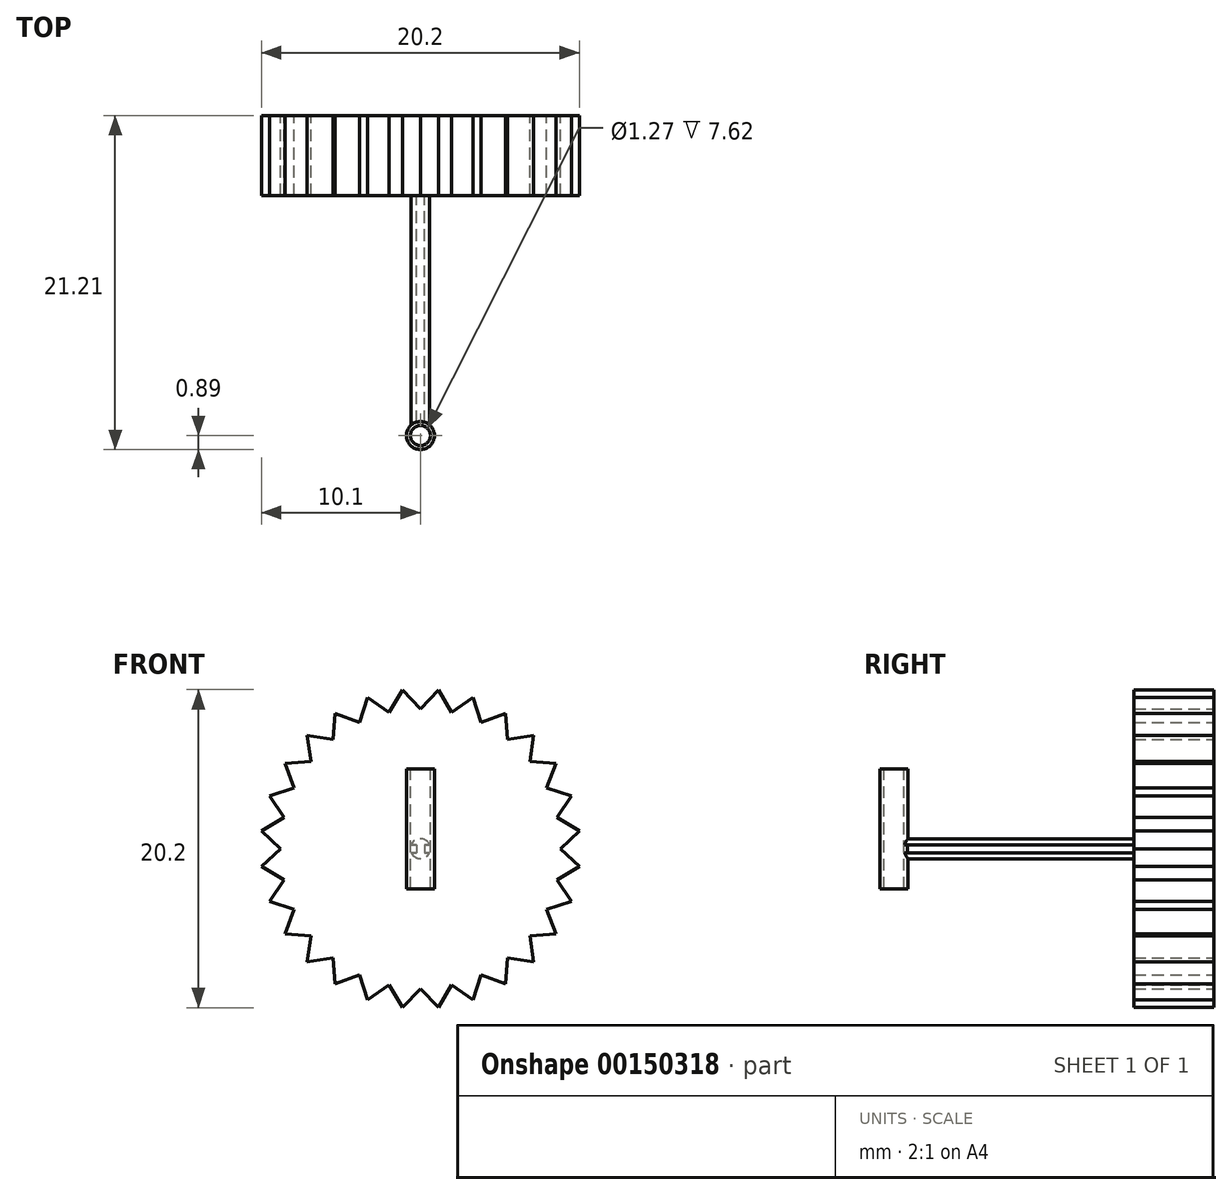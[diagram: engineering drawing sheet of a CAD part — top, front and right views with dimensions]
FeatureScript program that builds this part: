
annotation { "Feature Type Name" : "Feature", "Feature Type Description" : "" }
export const myFeature = defineFeature(function(context is Context, id is Id, definition is map)
    precondition{}
    {
        {
            var Q0;
            Q0=qCreatedBy(makeId("Front.planeOp"),FACE);
            var sketch = newSketch(context, id + "F0", { "sketchPlane" : qUnion([Q0])});
            skCircle(sketch, "E0", {"center": v(0, 0) * mm, "radius": 10.16 * mm});
            skCircle(sketch, "E1", {"center": v(0, 0) * mm, "radius": 8.9 * mm});
            skLineSegment(sketch, "E2", {"start": v(0, 0) * mm, "end": v(0, 8.9) * mm});
            skLineSegment(sketch, "E3", {"start": v(0, 8.9) * mm, "end": v(0, -8.9) * mm});
            skLineSegment(sketch, "E4", {"start": v(0, -8.9) * mm, "end": v(-1.14, -10.1) * mm});
            skLineSegment(sketch, "E5", {"start": v(-1.14, -10.1) * mm, "end": v(-1.98, -8.67) * mm});
            skLineSegment(sketch, "E6", {"start": v(-1.98, -8.67) * mm, "end": v(0, 0) * mm});
            skLineSegment(sketch, "E7", {"start": v(-1.14, -10.1) * mm, "end": v(0, 0) * mm});
            skLineSegment(sketch, "E8", {"start": v(0, 0) * mm, "end": v(-3.36, -9.59) * mm});
            skLineSegment(sketch, "E9", {"start": v(0, 0) * mm, "end": v(-3.86, -8) * mm});
            skLineSegment(sketch, "E10", {"start": v(-3.86, -8) * mm, "end": v(-3.36, -9.59) * mm});
            skLineSegment(sketch, "E11", {"start": v(-1.98, -8.67) * mm, "end": v(-3.36, -9.59) * mm});
            skLineSegment(sketch, "E12.MirrorCS", {"start": v(-3.86, -8) * mm, "end": v(-5.4, -8.6) * mm});
            skLineSegment(sketch, "E13.MirrorCS", {"start": v(0, 0) * mm, "end": v(-5.4, -8.6) * mm});
            skLineSegment(sketch, "E14.MirrorCS", {"start": v(-5.54, -6.95) * mm, "end": v(-5.4, -8.6) * mm});
            skLineSegment(sketch, "E15.MirrorCS", {"start": v(-7.18, -7.18) * mm, "end": v(-5.54, -6.95) * mm});
            skLineSegment(sketch, "E16.MirrorCS", {"start": v(-5.54, -6.95) * mm, "end": v(0, 0) * mm});
            skLineSegment(sketch, "E17.MirrorCS", {"start": v(-7.18, -7.18) * mm, "end": v(0, 0) * mm});
            skLineSegment(sketch, "E18.MirrorCS", {"start": v(-6.95, -5.54) * mm, "end": v(-7.18, -7.18) * mm});
            skLineSegment(sketch, "E19.MirrorCS", {"start": v(6.95, 5.54) * mm, "end": v(-6.95, -5.54) * mm});
            skLineSegment(sketch, "E20.MirrorCS", {"start": v(-6.95, -5.54) * mm, "end": v(-8.6, -5.4) * mm});
            skLineSegment(sketch, "E21.MirrorCS", {"start": v(-8.6, -5.4) * mm, "end": v(0, 0) * mm});
            skLineSegment(sketch, "E22.MirrorCS", {"start": v(-8.6, -5.4) * mm, "end": v(-8, -3.86) * mm});
            skLineSegment(sketch, "E23.MirrorCS", {"start": v(-8, -3.86) * mm, "end": v(0, 0) * mm});
            skLineSegment(sketch, "E24.MirrorCS", {"start": v(-8, -3.86) * mm, "end": v(-9.59, -3.36) * mm});
            skLineSegment(sketch, "E25.MirrorCS", {"start": v(0, 0) * mm, "end": v(-9.59, -3.36) * mm});
            skLineSegment(sketch, "E26.MirrorCS", {"start": v(-8.67, -1.98) * mm, "end": v(-9.59, -3.36) * mm});
            skLineSegment(sketch, "E27.MirrorCS", {"start": v(0, 0) * mm, "end": v(-8.67, -1.98) * mm});
            skLineSegment(sketch, "E28.MirrorCS", {"start": v(-8.67, -1.98) * mm, "end": v(-10.1, -1.14) * mm});
            skLineSegment(sketch, "E29.MirrorCS", {"start": v(0, 0) * mm, "end": v(-10.1, -1.14) * mm});
            skLineSegment(sketch, "E30.MirrorCS", {"start": v(-8.9, 0) * mm, "end": v(-10.1, -1.14) * mm});
            skLineSegment(sketch, "E31.MirrorCS", {"start": v(-8.9, 0) * mm, "end": v(0, 0) * mm});
            skLineSegment(sketch, "E32.MirrorCS", {"start": v(-10.1, 1.14) * mm, "end": v(-8.9, 0) * mm});
            skLineSegment(sketch, "E33.MirrorCS", {"start": v(-10.1, 1.14) * mm, "end": v(0, 0) * mm});
            skLineSegment(sketch, "E34.MirrorCS", {"start": v(-8.67, 1.98) * mm, "end": v(-10.1, 1.14) * mm});
            skLineSegment(sketch, "E35.MirrorCS", {"start": v(8.67, -1.98) * mm, "end": v(-8.67, 1.98) * mm});
            skLineSegment(sketch, "E36.MirrorCS", {"start": v(-8.67, 1.98) * mm, "end": v(-9.59, 3.36) * mm});
            skLineSegment(sketch, "E37.MirrorCS", {"start": v(-9.59, 3.36) * mm, "end": v(0, 0) * mm});
            skLineSegment(sketch, "E38.MirrorCS", {"start": v(-9.59, 3.36) * mm, "end": v(-8, 3.86) * mm});
            skLineSegment(sketch, "E39.MirrorCS", {"start": v(-8, 3.86) * mm, "end": v(0, 0) * mm});
            skLineSegment(sketch, "E40.MirrorCS", {"start": v(-8, 3.86) * mm, "end": v(-8.6, 5.4) * mm});
            skLineSegment(sketch, "E41.MirrorCS", {"start": v(0, 0) * mm, "end": v(-8.6, 5.4) * mm});
            skLineSegment(sketch, "E42.MirrorCS", {"start": v(-6.95, 5.54) * mm, "end": v(-8.6, 5.4) * mm});
            skLineSegment(sketch, "E43.MirrorCS", {"start": v(0, 0) * mm, "end": v(-6.95, 5.54) * mm});
            skLineSegment(sketch, "E44.MirrorCS", {"start": v(-6.95, 5.54) * mm, "end": v(-7.18, 7.18) * mm});
            skLineSegment(sketch, "E45.MirrorCS", {"start": v(0, 0) * mm, "end": v(-7.18, 7.18) * mm});
            skLineSegment(sketch, "E46.MirrorCS", {"start": v(-5.54, 6.95) * mm, "end": v(-7.18, 7.18) * mm});
            skLineSegment(sketch, "E47.MirrorCS", {"start": v(-5.54, 6.95) * mm, "end": v(0, 0) * mm});
            skLineSegment(sketch, "E48.MirrorCS", {"start": v(-5.4, 8.6) * mm, "end": v(-5.54, 6.95) * mm});
            skLineSegment(sketch, "E49.MirrorCS", {"start": v(-5.4, 8.6) * mm, "end": v(0, 0) * mm});
            skLineSegment(sketch, "E50.MirrorCS", {"start": v(-3.86, 8) * mm, "end": v(-5.4, 8.6) * mm});
            skLineSegment(sketch, "E51.MirrorCS", {"start": v(3.86, -8) * mm, "end": v(-3.86, 8) * mm});
            skLineSegment(sketch, "E52.MirrorCS", {"start": v(-3.86, 8) * mm, "end": v(-3.36, 9.59) * mm});
            skLineSegment(sketch, "E53.MirrorCS", {"start": v(-3.36, 9.59) * mm, "end": v(0, 0) * mm});
            skLineSegment(sketch, "E54.MirrorCS", {"start": v(-3.36, 9.59) * mm, "end": v(-1.98, 8.67) * mm});
            skLineSegment(sketch, "E55.MirrorCS", {"start": v(-1.98, 8.67) * mm, "end": v(0, 0) * mm});
            skLineSegment(sketch, "E56.MirrorCS", {"start": v(-1.98, 8.67) * mm, "end": v(-1.14, 10.1) * mm});
            skLineSegment(sketch, "E57.MirrorCS", {"start": v(0, 0) * mm, "end": v(-1.14, 10.1) * mm});
            skLineSegment(sketch, "E58.MirrorCS", {"start": v(0, 8.89) * mm, "end": v(-1.14, 10.1) * mm});
            skLineSegment(sketch, "E59.MirrorCS", {"start": v(0, 0) * mm, "end": v(0, 8.89) * mm});
            skLineSegment(sketch, "E60.MirrorCS", {"start": v(0, 8.89) * mm, "end": v(1.14, 10.1) * mm});
            skLineSegment(sketch, "E61.MirrorCS", {"start": v(0, 0) * mm, "end": v(1.14, 10.1) * mm});
            skLineSegment(sketch, "E62.MirrorCS", {"start": v(1.98, 8.67) * mm, "end": v(1.14, 10.1) * mm});
            skLineSegment(sketch, "E63.MirrorCS", {"start": v(1.98, 8.67) * mm, "end": v(0, 0) * mm});
            skLineSegment(sketch, "E64.MirrorCS", {"start": v(3.36, 9.59) * mm, "end": v(1.98, 8.67) * mm});
            skLineSegment(sketch, "E65.MirrorCS", {"start": v(3.36, 9.59) * mm, "end": v(0, 0) * mm});
            skLineSegment(sketch, "E66.MirrorCS", {"start": v(3.86, 8) * mm, "end": v(3.36, 9.59) * mm});
            skLineSegment(sketch, "E67.MirrorCS", {"start": v(-3.86, -8) * mm, "end": v(3.86, 8) * mm});
            skLineSegment(sketch, "E68.MirrorCS", {"start": v(3.86, 8) * mm, "end": v(5.4, 8.6) * mm});
            skLineSegment(sketch, "E69.MirrorCS", {"start": v(5.4, 8.6) * mm, "end": v(0, 0) * mm});
            skLineSegment(sketch, "E70.MirrorCS", {"start": v(5.4, 8.6) * mm, "end": v(5.54, 6.95) * mm});
            skLineSegment(sketch, "E71.MirrorCS", {"start": v(5.54, 6.95) * mm, "end": v(0, 0) * mm});
            skLineSegment(sketch, "E72.MirrorCS", {"start": v(5.54, 6.95) * mm, "end": v(7.18, 7.18) * mm});
            skLineSegment(sketch, "E73.MirrorCS", {"start": v(0, 0) * mm, "end": v(7.18, 7.18) * mm});
            skLineSegment(sketch, "E74.MirrorCS", {"start": v(6.95, 5.54) * mm, "end": v(7.18, 7.18) * mm});
            skLineSegment(sketch, "E75.MirrorCS", {"start": v(6.95, 5.54) * mm, "end": v(8.6, 5.4) * mm});
            skLineSegment(sketch, "E76.MirrorCS", {"start": v(0, 0) * mm, "end": v(8.6, 5.4) * mm});
            skLineSegment(sketch, "E77.MirrorCS", {"start": v(8, 3.86) * mm, "end": v(8.6, 5.4) * mm});
            skLineSegment(sketch, "E78.MirrorCS", {"start": v(8, 3.86) * mm, "end": v(0, 0) * mm});
            skLineSegment(sketch, "E79.MirrorCS", {"start": v(9.59, 3.36) * mm, "end": v(8, 3.86) * mm});
            skLineSegment(sketch, "E80.MirrorCS", {"start": v(9.59, 3.36) * mm, "end": v(0, 0) * mm});
            skLineSegment(sketch, "E81.MirrorCS", {"start": v(8.67, 1.98) * mm, "end": v(9.59, 3.36) * mm});
            skLineSegment(sketch, "E82.MirrorCS", {"start": v(-8.67, -1.98) * mm, "end": v(8.67, 1.98) * mm});
            skLineSegment(sketch, "E83.MirrorCS", {"start": v(8.67, 1.98) * mm, "end": v(10.1, 1.14) * mm});
            skLineSegment(sketch, "E84.MirrorCS", {"start": v(10.1, 1.14) * mm, "end": v(8.9, 0) * mm});
            skLineSegment(sketch, "E85.MirrorCS", {"start": v(10.1, 1.14) * mm, "end": v(0, 0) * mm});
            skLineSegment(sketch, "E86.MirrorCS", {"start": v(8.9, 0) * mm, "end": v(0, 0) * mm});
            skLineSegment(sketch, "E87.MirrorCS", {"start": v(8.9, 0) * mm, "end": v(10.1, -1.14) * mm});
            skLineSegment(sketch, "E88.MirrorCS", {"start": v(0, 0) * mm, "end": v(10.1, -1.14) * mm});
            skLineSegment(sketch, "E89.MirrorCS", {"start": v(8.67, -1.98) * mm, "end": v(10.1, -1.14) * mm});
            skLineSegment(sketch, "E90.MirrorCS", {"start": v(0, 0) * mm, "end": v(8.67, -1.98) * mm});
            skLineSegment(sketch, "E91.MirrorCS", {"start": v(8.67, -1.98) * mm, "end": v(9.59, -3.36) * mm});
            skLineSegment(sketch, "E92.MirrorCS", {"start": v(0, 0) * mm, "end": v(9.59, -3.36) * mm});
            skLineSegment(sketch, "E93.MirrorCS", {"start": v(8, -3.86) * mm, "end": v(9.59, -3.36) * mm});
            skLineSegment(sketch, "E94.MirrorCS", {"start": v(8, -3.86) * mm, "end": v(0, 0) * mm});
            skLineSegment(sketch, "E95.MirrorCS", {"start": v(8.6, -5.4) * mm, "end": v(8, -3.86) * mm});
            skLineSegment(sketch, "E96.MirrorCS", {"start": v(8.6, -5.4) * mm, "end": v(0, 0) * mm});
            skLineSegment(sketch, "E97.MirrorCS", {"start": v(6.95, -5.54) * mm, "end": v(8.6, -5.4) * mm});
            skLineSegment(sketch, "E98.MirrorCS", {"start": v(-6.95, 5.54) * mm, "end": v(6.95, -5.54) * mm});
            skLineSegment(sketch, "E99.MirrorCS", {"start": v(6.95, -5.54) * mm, "end": v(7.18, -7.18) * mm});
            skLineSegment(sketch, "E100.MirrorCS", {"start": v(7.18, -7.18) * mm, "end": v(0, 0) * mm});
            skLineSegment(sketch, "E101.MirrorCS", {"start": v(7.18, -7.18) * mm, "end": v(5.54, -6.95) * mm});
            skLineSegment(sketch, "E102.MirrorCS", {"start": v(5.54, -6.95) * mm, "end": v(0, 0) * mm});
            skLineSegment(sketch, "E103.MirrorCS", {"start": v(5.54, -6.95) * mm, "end": v(5.4, -8.6) * mm});
            skLineSegment(sketch, "E104.MirrorCS", {"start": v(0, 0) * mm, "end": v(5.4, -8.6) * mm});
            skLineSegment(sketch, "E105.MirrorCS", {"start": v(3.86, -8) * mm, "end": v(5.4, -8.6) * mm});
            skLineSegment(sketch, "E106.MirrorCS", {"start": v(0, 0) * mm, "end": v(3.86, -8) * mm});
            skLineSegment(sketch, "E107.MirrorCS", {"start": v(3.86, -8) * mm, "end": v(3.36, -9.59) * mm});
            skLineSegment(sketch, "E108.MirrorCS", {"start": v(1.98, -8.67) * mm, "end": v(3.36, -9.59) * mm});
            skLineSegment(sketch, "E109.MirrorCS", {"start": v(0, 0) * mm, "end": v(3.36, -9.59) * mm});
            skLineSegment(sketch, "E110.MirrorCS", {"start": v(1.98, -8.67) * mm, "end": v(0, 0) * mm});
            skLineSegment(sketch, "E111.MirrorCS", {"start": v(1.14, -10.1) * mm, "end": v(1.98, -8.67) * mm});
            skLineSegment(sketch, "E112.MirrorCS", {"start": v(1.14, -10.1) * mm, "end": v(0, 0) * mm});
            skLineSegment(sketch, "E113.MirrorCS", {"start": v(0, -8.9) * mm, "end": v(1.14, -10.1) * mm});
            skSolve(sketch);
        }
        {
            var Q0;
            {var subQ0=sQuery(id+"F0.wireOp",EDGE,"E51.MirrorCS");Q0=makeQuery(id+"F0.imprint","IMPRINT",FACE,{"disambiguationData":[TD([[makeQuery(id+"F0.imprint","IMPRINT",EDGE,{"derivedFrom":subQ0}),1.0]])]});}
            var Q1;
            {var subQ0=sQuery(id+"F0.wireOp",EDGE,"E47.MirrorCS");Q1=makeQuery(id+"F0.imprint","IMPRINT",FACE,{"disambiguationData":[TD([[makeQuery(id+"F0.imprint","IMPRINT",EDGE,{"derivedFrom":subQ0}),1.0]])]});}
            var Q2;
            {var subQ0=sQuery(id+"F0.wireOp",EDGE,"E48.MirrorCS");Q2=makeQuery(id+"F0.imprint","IMPRINT",FACE,{"disambiguationData":[TD([[makeQuery(id+"F0.imprint","IMPRINT",EDGE,{"derivedFrom":subQ0}),1.0]])]});}
            var Q3;
            {var subQ0=sQuery(id+"F0.wireOp",EDGE,"E50.MirrorCS");Q3=makeQuery(id+"F0.imprint","IMPRINT",FACE,{"disambiguationData":[TD([[makeQuery(id+"F0.imprint","IMPRINT",EDGE,{"derivedFrom":subQ0}),1.0]])]});}
            var Q4;
            {var subQ0=sQuery(id+"F0.wireOp",EDGE,"E52.MirrorCS");Q4=makeQuery(id+"F0.imprint","IMPRINT",FACE,{"disambiguationData":[TD([[makeQuery(id+"F0.imprint","IMPRINT",EDGE,{"derivedFrom":subQ0}),-1.0]])]});}
            var Q5;
            {var subQ0=sQuery(id+"F0.wireOp",EDGE,"E54.MirrorCS");Q5=makeQuery(id+"F0.imprint","IMPRINT",FACE,{"disambiguationData":[TD([[makeQuery(id+"F0.imprint","IMPRINT",EDGE,{"derivedFrom":subQ0}),-1.0]])]});}
            var Q6;
            {var subQ0=sQuery(id+"F0.wireOp",EDGE,"E55.MirrorCS");Q6=makeQuery(id+"F0.imprint","IMPRINT",FACE,{"disambiguationData":[TD([[makeQuery(id+"F0.imprint","IMPRINT",EDGE,{"derivedFrom":subQ0}),-1.0]])]});}
            var Q7;
            {var subQ0=sQuery(id+"F0.wireOp",EDGE,"E51.MirrorCS");Q7=makeQuery(id+"F0.imprint","IMPRINT",FACE,{"disambiguationData":[TD([[makeQuery(id+"F0.imprint","IMPRINT",EDGE,{"derivedFrom":subQ0}),-1.0]])]});}
            var Q8;
            {var subQ1=sQuery(id+"F0.wireOp",EDGE,"E1");var subQ3=sQuery(id+"F0.wireOp",EDGE,"E57.MirrorCS");var subQ4=makeQuery(id+"F0.imprint","INTERSECT",VERTEX,{"derivedFrom":[subQ1,subQ3]});Q8=makeQuery(id+"F0.imprint","IMPRINT",FACE,{"disambiguationData":[TD([[makeQuery(id+"F0.imprint","IMPRINT",EDGE,{"disambiguationData":[TD([[subQ4,1.0]])],"derivedFrom":subQ1}),1.0]])]});}
            var Q9;
            {var subQ0=sQuery(id+"F0.wireOp",EDGE,"E58.MirrorCS");Q9=makeQuery(id+"F0.imprint","IMPRINT",FACE,{"disambiguationData":[TD([[makeQuery(id+"F0.imprint","IMPRINT",EDGE,{"derivedFrom":subQ0}),1.0]])]});}
            var Q10;
            {var subQ0=sQuery(id+"F0.wireOp",EDGE,"E56.MirrorCS");Q10=makeQuery(id+"F0.imprint","IMPRINT",FACE,{"disambiguationData":[TD([[makeQuery(id+"F0.imprint","IMPRINT",EDGE,{"derivedFrom":subQ0}),-1.0]])]});}
            var Q11;
            {var subQ0=sQuery(id+"F0.wireOp",EDGE,"E55.MirrorCS");Q11=makeQuery(id+"F0.imprint","IMPRINT",FACE,{"disambiguationData":[TD([[makeQuery(id+"F0.imprint","IMPRINT",EDGE,{"derivedFrom":subQ0}),1.0]])]});}
            var Q12;
            {var subQ0=sQuery(id+"F0.wireOp",EDGE,"E47.MirrorCS");Q12=makeQuery(id+"F0.imprint","IMPRINT",FACE,{"disambiguationData":[TD([[makeQuery(id+"F0.imprint","IMPRINT",EDGE,{"derivedFrom":subQ0}),-1.0]])]});}
            var Q13;
            {var subQ0=sQuery(id+"F0.wireOp",EDGE,"E46.MirrorCS");Q13=makeQuery(id+"F0.imprint","IMPRINT",FACE,{"disambiguationData":[TD([[makeQuery(id+"F0.imprint","IMPRINT",EDGE,{"derivedFrom":subQ0}),1.0]])]});}
            var Q14;
            {var subQ1=sQuery(id+"F0.wireOp",EDGE,"E1");var subQ3=sQuery(id+"F0.wireOp",EDGE,"E45.MirrorCS");var subQ4=makeQuery(id+"F0.imprint","INTERSECT",VERTEX,{"derivedFrom":[subQ1,subQ3]});Q14=makeQuery(id+"F0.imprint","IMPRINT",FACE,{"disambiguationData":[TD([[makeQuery(id+"F0.imprint","IMPRINT",EDGE,{"disambiguationData":[TD([[subQ4,-1.0]])],"derivedFrom":subQ1}),1.0]])]});}
            var Q15;
            {var subQ0=sQuery(id+"F0.wireOp",EDGE,"E44.MirrorCS");Q15=makeQuery(id+"F0.imprint","IMPRINT",FACE,{"disambiguationData":[TD([[makeQuery(id+"F0.imprint","IMPRINT",EDGE,{"derivedFrom":subQ0}),-1.0]])]});}
            var Q16;
            {var subQ1=sQuery(id+"F0.wireOp",EDGE,"E1");var subQ3=sQuery(id+"F0.wireOp",EDGE,"E41.MirrorCS");var subQ4=makeQuery(id+"F0.imprint","INTERSECT",VERTEX,{"derivedFrom":[subQ1,subQ3]});Q16=makeQuery(id+"F0.imprint","IMPRINT",FACE,{"disambiguationData":[TD([[makeQuery(id+"F0.imprint","IMPRINT",EDGE,{"disambiguationData":[TD([[subQ4,1.0]])],"derivedFrom":subQ1}),1.0]])]});}
            var Q17;
            {var subQ0=sQuery(id+"F0.wireOp",EDGE,"E42.MirrorCS");Q17=makeQuery(id+"F0.imprint","IMPRINT",FACE,{"disambiguationData":[TD([[makeQuery(id+"F0.imprint","IMPRINT",EDGE,{"derivedFrom":subQ0}),1.0]])]});}
            var Q18;
            {var subQ0=sQuery(id+"F0.wireOp",EDGE,"E40.MirrorCS");Q18=makeQuery(id+"F0.imprint","IMPRINT",FACE,{"disambiguationData":[TD([[makeQuery(id+"F0.imprint","IMPRINT",EDGE,{"derivedFrom":subQ0}),-1.0]])]});}
            var Q19;
            {var subQ0=sQuery(id+"F0.wireOp",EDGE,"E39.MirrorCS");Q19=makeQuery(id+"F0.imprint","IMPRINT",FACE,{"disambiguationData":[TD([[makeQuery(id+"F0.imprint","IMPRINT",EDGE,{"derivedFrom":subQ0}),1.0]])]});}
            var Q20;
            {var subQ0=sQuery(id+"F0.wireOp",EDGE,"E39.MirrorCS");Q20=makeQuery(id+"F0.imprint","IMPRINT",FACE,{"disambiguationData":[TD([[makeQuery(id+"F0.imprint","IMPRINT",EDGE,{"derivedFrom":subQ0}),-1.0]])]});}
            var Q21;
            {var subQ0=sQuery(id+"F0.wireOp",EDGE,"E38.MirrorCS");Q21=makeQuery(id+"F0.imprint","IMPRINT",FACE,{"disambiguationData":[TD([[makeQuery(id+"F0.imprint","IMPRINT",EDGE,{"derivedFrom":subQ0}),-1.0]])]});}
            var Q22;
            {var subQ0=sQuery(id+"F0.wireOp",EDGE,"E36.MirrorCS");Q22=makeQuery(id+"F0.imprint","IMPRINT",FACE,{"disambiguationData":[TD([[makeQuery(id+"F0.imprint","IMPRINT",EDGE,{"derivedFrom":subQ0}),-1.0]])]});}
            var Q23;
            {var subQ0=sQuery(id+"F0.wireOp",EDGE,"E35.MirrorCS");Q23=makeQuery(id+"F0.imprint","IMPRINT",FACE,{"disambiguationData":[TD([[makeQuery(id+"F0.imprint","IMPRINT",EDGE,{"derivedFrom":subQ0}),-1.0]])]});}
            var Q24;
            {var subQ0=sQuery(id+"F0.wireOp",EDGE,"E35.MirrorCS");Q24=makeQuery(id+"F0.imprint","IMPRINT",FACE,{"disambiguationData":[TD([[makeQuery(id+"F0.imprint","IMPRINT",EDGE,{"derivedFrom":subQ0}),1.0]])]});}
            var Q25;
            {var subQ0=sQuery(id+"F0.wireOp",EDGE,"E34.MirrorCS");Q25=makeQuery(id+"F0.imprint","IMPRINT",FACE,{"disambiguationData":[TD([[makeQuery(id+"F0.imprint","IMPRINT",EDGE,{"derivedFrom":subQ0}),1.0]])]});}
            var Q26;
            {var subQ0=sQuery(id+"F0.wireOp",EDGE,"E32.MirrorCS");Q26=makeQuery(id+"F0.imprint","IMPRINT",FACE,{"disambiguationData":[TD([[makeQuery(id+"F0.imprint","IMPRINT",EDGE,{"derivedFrom":subQ0}),1.0]])]});}
            var Q27;
            {var subQ0=sQuery(id+"F0.wireOp",EDGE,"E31.MirrorCS");Q27=makeQuery(id+"F0.imprint","IMPRINT",FACE,{"disambiguationData":[TD([[makeQuery(id+"F0.imprint","IMPRINT",EDGE,{"derivedFrom":subQ0}),1.0]])]});}
            var Q28;
            {var subQ0=sQuery(id+"F0.wireOp",EDGE,"E31.MirrorCS");Q28=makeQuery(id+"F0.imprint","IMPRINT",FACE,{"disambiguationData":[TD([[makeQuery(id+"F0.imprint","IMPRINT",EDGE,{"derivedFrom":subQ0}),-1.0]])]});}
            var Q29;
            {var subQ0=sQuery(id+"F0.wireOp",EDGE,"E30.MirrorCS");Q29=makeQuery(id+"F0.imprint","IMPRINT",FACE,{"disambiguationData":[TD([[makeQuery(id+"F0.imprint","IMPRINT",EDGE,{"derivedFrom":subQ0}),1.0]])]});}
            var Q30;
            {var subQ0=sQuery(id+"F0.wireOp",EDGE,"E28.MirrorCS");Q30=makeQuery(id+"F0.imprint","IMPRINT",FACE,{"disambiguationData":[TD([[makeQuery(id+"F0.imprint","IMPRINT",EDGE,{"derivedFrom":subQ0}),-1.0]])]});}
            var Q31;
            {var subQ1=sQuery(id+"F0.wireOp",EDGE,"E1");var subQ3=sQuery(id+"F0.wireOp",EDGE,"E29.MirrorCS");var subQ4=makeQuery(id+"F0.imprint","INTERSECT",VERTEX,{"derivedFrom":[subQ1,subQ3]});Q31=makeQuery(id+"F0.imprint","IMPRINT",FACE,{"disambiguationData":[TD([[makeQuery(id+"F0.imprint","IMPRINT",EDGE,{"disambiguationData":[TD([[subQ4,-1.0]])],"derivedFrom":subQ1}),1.0]])]});}
            var Q32;
            {var subQ1=sQuery(id+"F0.wireOp",EDGE,"E1");var subQ3=sQuery(id+"F0.wireOp",EDGE,"E25.MirrorCS");var subQ4=makeQuery(id+"F0.imprint","INTERSECT",VERTEX,{"derivedFrom":[subQ1,subQ3]});Q32=makeQuery(id+"F0.imprint","IMPRINT",FACE,{"disambiguationData":[TD([[makeQuery(id+"F0.imprint","IMPRINT",EDGE,{"disambiguationData":[TD([[subQ4,1.0]])],"derivedFrom":subQ1}),1.0]])]});}
            var Q33;
            {var subQ0=sQuery(id+"F0.wireOp",EDGE,"E26.MirrorCS");Q33=makeQuery(id+"F0.imprint","IMPRINT",FACE,{"disambiguationData":[TD([[makeQuery(id+"F0.imprint","IMPRINT",EDGE,{"derivedFrom":subQ0}),1.0]])]});}
            var Q34;
            {var subQ0=sQuery(id+"F0.wireOp",EDGE,"E24.MirrorCS");Q34=makeQuery(id+"F0.imprint","IMPRINT",FACE,{"disambiguationData":[TD([[makeQuery(id+"F0.imprint","IMPRINT",EDGE,{"derivedFrom":subQ0}),-1.0]])]});}
            var Q35;
            {var subQ0=sQuery(id+"F0.wireOp",EDGE,"E23.MirrorCS");Q35=makeQuery(id+"F0.imprint","IMPRINT",FACE,{"disambiguationData":[TD([[makeQuery(id+"F0.imprint","IMPRINT",EDGE,{"derivedFrom":subQ0}),1.0]])]});}
            var Q36;
            {var subQ0=sQuery(id+"F0.wireOp",EDGE,"E23.MirrorCS");Q36=makeQuery(id+"F0.imprint","IMPRINT",FACE,{"disambiguationData":[TD([[makeQuery(id+"F0.imprint","IMPRINT",EDGE,{"derivedFrom":subQ0}),-1.0]])]});}
            var Q37;
            {var subQ0=sQuery(id+"F0.wireOp",EDGE,"E22.MirrorCS");Q37=makeQuery(id+"F0.imprint","IMPRINT",FACE,{"disambiguationData":[TD([[makeQuery(id+"F0.imprint","IMPRINT",EDGE,{"derivedFrom":subQ0}),-1.0]])]});}
            var Q38;
            {var subQ0=sQuery(id+"F0.wireOp",EDGE,"E20.MirrorCS");Q38=makeQuery(id+"F0.imprint","IMPRINT",FACE,{"disambiguationData":[TD([[makeQuery(id+"F0.imprint","IMPRINT",EDGE,{"derivedFrom":subQ0}),-1.0]])]});}
            var Q39;
            {var subQ1=sQuery(id+"F0.wireOp",EDGE,"E1");var subQ3=sQuery(id+"F0.wireOp",EDGE,"E21.MirrorCS");var subQ4=makeQuery(id+"F0.imprint","INTERSECT",VERTEX,{"derivedFrom":[subQ1,subQ3]});Q39=makeQuery(id+"F0.imprint","IMPRINT",FACE,{"disambiguationData":[TD([[makeQuery(id+"F0.imprint","IMPRINT",EDGE,{"disambiguationData":[TD([[subQ4,-1.0]])],"derivedFrom":subQ1}),1.0]])]});}
            var Q40;
            {var subQ1=sQuery(id+"F0.wireOp",EDGE,"E1");var subQ3=sQuery(id+"F0.wireOp",EDGE,"E17.MirrorCS");var subQ4=makeQuery(id+"F0.imprint","INTERSECT",VERTEX,{"derivedFrom":[subQ1,subQ3]});Q40=makeQuery(id+"F0.imprint","IMPRINT",FACE,{"disambiguationData":[TD([[makeQuery(id+"F0.imprint","IMPRINT",EDGE,{"disambiguationData":[TD([[subQ4,1.0]])],"derivedFrom":subQ1}),1.0]])]});}
            var Q41;
            {var subQ0=sQuery(id+"F0.wireOp",EDGE,"E16.MirrorCS");Q41=makeQuery(id+"F0.imprint","IMPRINT",FACE,{"disambiguationData":[TD([[makeQuery(id+"F0.imprint","IMPRINT",EDGE,{"derivedFrom":subQ0}),1.0]])]});}
            var Q42;
            {var subQ0=sQuery(id+"F0.wireOp",EDGE,"E16.MirrorCS");Q42=makeQuery(id+"F0.imprint","IMPRINT",FACE,{"disambiguationData":[TD([[makeQuery(id+"F0.imprint","IMPRINT",EDGE,{"derivedFrom":subQ0}),-1.0]])]});}
            var Q43;
            {var subQ0=sQuery(id+"F0.wireOp",EDGE,"E18.MirrorCS");Q43=makeQuery(id+"F0.imprint","IMPRINT",FACE,{"disambiguationData":[TD([[makeQuery(id+"F0.imprint","IMPRINT",EDGE,{"derivedFrom":subQ0}),1.0]])]});}
            var Q44;
            {var subQ0=sQuery(id+"F0.wireOp",EDGE,"E15.MirrorCS");Q44=makeQuery(id+"F0.imprint","IMPRINT",FACE,{"disambiguationData":[TD([[makeQuery(id+"F0.imprint","IMPRINT",EDGE,{"derivedFrom":subQ0}),1.0]])]});}
            var Q45;
            {var subQ0=sQuery(id+"F0.wireOp",EDGE,"E14.MirrorCS");Q45=makeQuery(id+"F0.imprint","IMPRINT",FACE,{"disambiguationData":[TD([[makeQuery(id+"F0.imprint","IMPRINT",EDGE,{"derivedFrom":subQ0}),1.0]])]});}
            var Q46;
            {var subQ0=sQuery(id+"F0.wireOp",EDGE,"E12.MirrorCS");Q46=makeQuery(id+"F0.imprint","IMPRINT",FACE,{"disambiguationData":[TD([[makeQuery(id+"F0.imprint","IMPRINT",EDGE,{"derivedFrom":subQ0}),-1.0]])]});}
            var Q47;
            {var subQ1=sQuery(id+"F0.wireOp",EDGE,"E1");var subQ3=sQuery(id+"F0.wireOp",EDGE,"E8");var subQ4=makeQuery(id+"F0.imprint","INTERSECT",VERTEX,{"derivedFrom":[subQ1,subQ3]});Q47=makeQuery(id+"F0.imprint","IMPRINT",FACE,{"disambiguationData":[TD([[makeQuery(id+"F0.imprint","IMPRINT",EDGE,{"disambiguationData":[TD([[subQ4,1.0]])],"derivedFrom":subQ1}),1.0]])]});}
            var Q48;
            {var subQ0=sQuery(id+"F0.wireOp",EDGE,"E10");Q48=makeQuery(id+"F0.imprint","IMPRINT",FACE,{"disambiguationData":[TD([[makeQuery(id+"F0.imprint","IMPRINT",EDGE,{"derivedFrom":subQ0}),1.0]])]});}
            var Q49;
            {var subQ0=sQuery(id+"F0.wireOp",EDGE,"E11");Q49=makeQuery(id+"F0.imprint","IMPRINT",FACE,{"disambiguationData":[TD([[makeQuery(id+"F0.imprint","IMPRINT",EDGE,{"derivedFrom":subQ0}),-1.0]])]});}
            var Q50;
            {var subQ0=sQuery(id+"F0.wireOp",EDGE,"E6");Q50=makeQuery(id+"F0.imprint","IMPRINT",FACE,{"disambiguationData":[TD([[makeQuery(id+"F0.imprint","IMPRINT",EDGE,{"derivedFrom":subQ0}),1.0]])]});}
            var Q51;
            {var subQ0=sQuery(id+"F0.wireOp",EDGE,"E6");Q51=makeQuery(id+"F0.imprint","IMPRINT",FACE,{"disambiguationData":[TD([[makeQuery(id+"F0.imprint","IMPRINT",EDGE,{"derivedFrom":subQ0}),-1.0]])]});}
            var Q52;
            {var subQ0=sQuery(id+"F0.wireOp",EDGE,"E4");Q52=makeQuery(id+"F0.imprint","IMPRINT",FACE,{"disambiguationData":[TD([[makeQuery(id+"F0.imprint","IMPRINT",EDGE,{"derivedFrom":subQ0}),-1.0]])]});}
            var Q53;
            {var subQ0=sQuery(id+"F0.wireOp",EDGE,"E5");Q53=makeQuery(id+"F0.imprint","IMPRINT",FACE,{"disambiguationData":[TD([[makeQuery(id+"F0.imprint","IMPRINT",EDGE,{"derivedFrom":subQ0}),-1.0]])]});}
            var Q54;
            {var subQ1=sQuery(id+"F0.wireOp",EDGE,"E1");var subQ3=sQuery(id+"F0.wireOp",EDGE,"E7");var subQ4=makeQuery(id+"F0.imprint","INTERSECT",VERTEX,{"derivedFrom":[subQ1,subQ3]});Q54=makeQuery(id+"F0.imprint","IMPRINT",FACE,{"disambiguationData":[TD([[makeQuery(id+"F0.imprint","IMPRINT",EDGE,{"disambiguationData":[TD([[subQ4,-1.0]])],"derivedFrom":subQ1}),1.0]])]});}
            var Q55;
            {var subQ1=sQuery(id+"F0.wireOp",EDGE,"E1");var subQ3=sQuery(id+"F0.wireOp",EDGE,"E13.MirrorCS");var subQ4=makeQuery(id+"F0.imprint","INTERSECT",VERTEX,{"derivedFrom":[subQ1,subQ3]});Q55=makeQuery(id+"F0.imprint","IMPRINT",FACE,{"disambiguationData":[TD([[makeQuery(id+"F0.imprint","IMPRINT",EDGE,{"disambiguationData":[TD([[subQ4,-1.0]])],"derivedFrom":subQ1}),1.0]])]});}
            extrude(context, id + "F1", {"entities" : qUnion([Q0, Q1, Q2, Q3, Q4, Q5, Q6, Q7, Q8, Q9, Q10, Q11, Q12, Q13, Q14, Q15, Q16, Q17, Q18, Q19, Q20, Q21, Q22, Q23, Q24, Q25, Q26, Q27, Q28, Q29, Q30, Q31, Q32, Q33, Q34, Q35, Q36, Q37, Q38, Q39, Q40, Q41, Q42, Q43, Q44, Q45, Q46, Q47, Q48, Q49, Q50, Q51, Q52, Q53, Q54, Q55]), "depth" : 5.08 * mm});
        }
        {
            var Q0;
            Q0=makeQuery(id+"F1.opExtrude","SWEPT_BODY",BODY,{"disambiguationData":[OSD([sQuery(id+"F0.wireOp",EDGE,"E4"),sQuery(id+"F0.wireOp",EDGE,"E5"),sQuery(id+"F0.wireOp",EDGE,"E10"),sQuery(id+"F0.wireOp",EDGE,"E11"),sQuery(id+"F0.wireOp",EDGE,"E12.MirrorCS"),sQuery(id+"F0.wireOp",EDGE,"E14.MirrorCS"),sQuery(id+"F0.wireOp",EDGE,"E15.MirrorCS"),sQuery(id+"F0.wireOp",EDGE,"E18.MirrorCS"),sQuery(id+"F0.wireOp",EDGE,"E20.MirrorCS"),sQuery(id+"F0.wireOp",EDGE,"E22.MirrorCS"),sQuery(id+"F0.wireOp",EDGE,"E24.MirrorCS"),sQuery(id+"F0.wireOp",EDGE,"E26.MirrorCS"),sQuery(id+"F0.wireOp",EDGE,"E28.MirrorCS"),sQuery(id+"F0.wireOp",EDGE,"E30.MirrorCS"),sQuery(id+"F0.wireOp",EDGE,"E32.MirrorCS"),sQuery(id+"F0.wireOp",EDGE,"E34.MirrorCS"),sQuery(id+"F0.wireOp",EDGE,"E36.MirrorCS"),sQuery(id+"F0.wireOp",EDGE,"E38.MirrorCS"),sQuery(id+"F0.wireOp",EDGE,"E40.MirrorCS"),sQuery(id+"F0.wireOp",EDGE,"E42.MirrorCS"),sQuery(id+"F0.wireOp",EDGE,"E44.MirrorCS"),sQuery(id+"F0.wireOp",EDGE,"E46.MirrorCS"),sQuery(id+"F0.wireOp",EDGE,"E48.MirrorCS"),sQuery(id+"F0.wireOp",EDGE,"E50.MirrorCS"),sQuery(id+"F0.wireOp",EDGE,"E52.MirrorCS"),sQuery(id+"F0.wireOp",EDGE,"E54.MirrorCS"),sQuery(id+"F0.wireOp",EDGE,"E56.MirrorCS"),sQuery(id+"F0.wireOp",EDGE,"E58.MirrorCS"),sQuery(id+"F0.wireOp",EDGE,"E3")])]});
            var Q1;
            Q1=qCreatedBy(makeId("Right.planeOp"),FACE);
            mirror(context, id + "F2", {"operationType" : NewBodyOperationType.ADD, "entities" : qUnion([Q0]), "mirrorPlane" : qUnion([Q1])});
        }
        {
            var Q0;
            {var subQ0=makeQuery(id+"F1.opExtrude","CAP_FACE",FACE,{"disambiguationData":[OSD([sQuery(id+"F0.wireOp",EDGE,"E4"),sQuery(id+"F0.wireOp",EDGE,"E5"),sQuery(id+"F0.wireOp",EDGE,"E10"),sQuery(id+"F0.wireOp",EDGE,"E11"),sQuery(id+"F0.wireOp",EDGE,"E12.MirrorCS"),sQuery(id+"F0.wireOp",EDGE,"E14.MirrorCS"),sQuery(id+"F0.wireOp",EDGE,"E15.MirrorCS"),sQuery(id+"F0.wireOp",EDGE,"E18.MirrorCS"),sQuery(id+"F0.wireOp",EDGE,"E20.MirrorCS"),sQuery(id+"F0.wireOp",EDGE,"E22.MirrorCS"),sQuery(id+"F0.wireOp",EDGE,"E24.MirrorCS"),sQuery(id+"F0.wireOp",EDGE,"E26.MirrorCS"),sQuery(id+"F0.wireOp",EDGE,"E28.MirrorCS"),sQuery(id+"F0.wireOp",EDGE,"E30.MirrorCS"),sQuery(id+"F0.wireOp",EDGE,"E32.MirrorCS"),sQuery(id+"F0.wireOp",EDGE,"E34.MirrorCS"),sQuery(id+"F0.wireOp",EDGE,"E36.MirrorCS"),sQuery(id+"F0.wireOp",EDGE,"E38.MirrorCS"),sQuery(id+"F0.wireOp",EDGE,"E40.MirrorCS"),sQuery(id+"F0.wireOp",EDGE,"E42.MirrorCS"),sQuery(id+"F0.wireOp",EDGE,"E44.MirrorCS"),sQuery(id+"F0.wireOp",EDGE,"E46.MirrorCS"),sQuery(id+"F0.wireOp",EDGE,"E48.MirrorCS"),sQuery(id+"F0.wireOp",EDGE,"E50.MirrorCS"),sQuery(id+"F0.wireOp",EDGE,"E52.MirrorCS"),sQuery(id+"F0.wireOp",EDGE,"E54.MirrorCS"),sQuery(id+"F0.wireOp",EDGE,"E56.MirrorCS"),sQuery(id+"F0.wireOp",EDGE,"E58.MirrorCS"),sQuery(id+"F0.wireOp",EDGE,"E3")])],"isStart":false});Q0=makeQuery(id+"F2.boolean.opBoolean","MERGE",FACE,{"derivedFrom":[subQ0,makeQuery(id+"F2.opPattern","COPY",FACE,{"derivedFrom":subQ0,"instanceName":"1"})]});}
            var sketch = newSketch(context, id + "F3", { "sketchPlane" : qUnion([Q0])});
            skCircle(sketch, "E114", {"center": v(0, 0) * mm, "radius": 0.64 * mm});
            skLineSegment(sketch, "E115.bottom", {"start": v(1.18, 0.25) * mm, "end": v(-1.18, 0.25) * mm});
            skLineSegment(sketch, "E115.top", {"start": v(1.18, -0.25) * mm, "end": v(-1.18, -0.25) * mm});
            skLineSegment(sketch, "E115.left", {"start": v(1.18, 0.25) * mm, "end": v(1.18, -0.25) * mm});
            skLineSegment(sketch, "E115.right", {"start": v(-1.18, 0.25) * mm, "end": v(-1.18, -0.25) * mm});
            skLineSegment(sketch, "E116.bottom", {"start": v(0.25, 1.07) * mm, "end": v(-0.25, 1.07) * mm});
            skLineSegment(sketch, "E116.top", {"start": v(0.25, -1.07) * mm, "end": v(-0.25, -1.07) * mm});
            skLineSegment(sketch, "E116.left", {"start": v(0.25, 1.07) * mm, "end": v(0.25, -1.07) * mm});
            skLineSegment(sketch, "E116.right", {"start": v(-0.25, 1.07) * mm, "end": v(-0.25, -1.07) * mm});
            skSolve(sketch);
        }
        {
            var Q0;
            {var subQ0=sQuery(id+"F3.wireOp",EDGE,"E116.left");var subQ1=sQuery(id+"F3.wireOp",EDGE,"E114");var subQ2=makeQuery(id+"F3.imprint","INTERSECT",VERTEX,{"disambiguationData":[OD(0.0)],"derivedFrom":[subQ1,subQ0]});Q0=makeQuery(id+"F3.imprint","IMPRINT",FACE,{"disambiguationData":[TD([[makeQuery(id+"F3.imprint","IMPRINT",EDGE,{"disambiguationData":[TD([[subQ2,-1.0]])],"derivedFrom":subQ1}),1.0]])]});}
            var Q1;
            {var subQ0=sQuery(id+"F3.wireOp",EDGE,"E115.bottom");var subQ1=sQuery(id+"F3.wireOp",EDGE,"E114");var subQ2=makeQuery(id+"F3.imprint","INTERSECT",VERTEX,{"disambiguationData":[OD(1.0)],"derivedFrom":[subQ1,subQ0]});Q1=makeQuery(id+"F3.imprint","IMPRINT",FACE,{"disambiguationData":[TD([[makeQuery(id+"F3.imprint","IMPRINT",EDGE,{"disambiguationData":[TD([[subQ2,-1.0]])],"derivedFrom":subQ1}),1.0]])]});}
            var Q2;
            {var subQ0=sQuery(id+"F3.wireOp",EDGE,"E116.left");var subQ1=sQuery(id+"F3.wireOp",EDGE,"E115.bottom");var subQ2=makeQuery(id+"F3.imprint","INTERSECT",VERTEX,{"derivedFrom":[subQ1,subQ0]});Q2=makeQuery(id+"F3.imprint","IMPRINT",FACE,{"disambiguationData":[TD([[makeQuery(id+"F3.imprint","IMPRINT",EDGE,{"disambiguationData":[TD([[subQ2,-1.0]])],"derivedFrom":subQ1}),1.0]])]});}
            var Q3;
            {var subQ0=sQuery(id+"F3.wireOp",EDGE,"E115.bottom");var subQ1=sQuery(id+"F3.wireOp",EDGE,"E114");var subQ2=makeQuery(id+"F3.imprint","INTERSECT",VERTEX,{"disambiguationData":[OD(0.0)],"derivedFrom":[subQ1,subQ0]});Q3=makeQuery(id+"F3.imprint","IMPRINT",FACE,{"disambiguationData":[TD([[makeQuery(id+"F3.imprint","IMPRINT",EDGE,{"disambiguationData":[TD([[subQ2,1.0]])],"derivedFrom":subQ1}),1.0]])]});}
            var Q4;
            {var subQ0=sQuery(id+"F3.wireOp",EDGE,"E116.right");var subQ1=sQuery(id+"F3.wireOp",EDGE,"E114");var subQ2=makeQuery(id+"F3.imprint","INTERSECT",VERTEX,{"disambiguationData":[OD(1.0)],"derivedFrom":[subQ1,subQ0]});Q4=makeQuery(id+"F3.imprint","IMPRINT",FACE,{"disambiguationData":[TD([[makeQuery(id+"F3.imprint","IMPRINT",EDGE,{"disambiguationData":[TD([[subQ2,-1.0]])],"derivedFrom":subQ1}),1.0]])]});}
            var Q5;
            {var subQ0=sQuery(id+"F3.wireOp",EDGE,"E116.right");var subQ1=sQuery(id+"F3.wireOp",EDGE,"E114");var subQ2=makeQuery(id+"F3.imprint","INTERSECT",VERTEX,{"disambiguationData":[OD(0.0)],"derivedFrom":[subQ1,subQ0]});Q5=makeQuery(id+"F3.imprint","IMPRINT",FACE,{"disambiguationData":[TD([[makeQuery(id+"F3.imprint","IMPRINT",EDGE,{"disambiguationData":[TD([[subQ2,-1.0]])],"derivedFrom":subQ1}),1.0]])]});}
            var Q6;
            {var subQ0=sQuery(id+"F3.wireOp",EDGE,"E116.left");var subQ1=sQuery(id+"F3.wireOp",EDGE,"E114");var subQ2=makeQuery(id+"F3.imprint","INTERSECT",VERTEX,{"disambiguationData":[OD(0.0)],"derivedFrom":[subQ1,subQ0]});Q6=makeQuery(id+"F3.imprint","IMPRINT",FACE,{"disambiguationData":[TD([[makeQuery(id+"F3.imprint","IMPRINT",EDGE,{"disambiguationData":[TD([[subQ2,1.0]])],"derivedFrom":subQ1}),1.0]])]});}
            var Q7;
            {var subQ0=sQuery(id+"F3.wireOp",EDGE,"E116.left");var subQ1=sQuery(id+"F3.wireOp",EDGE,"E114");var subQ2=makeQuery(id+"F3.imprint","INTERSECT",VERTEX,{"disambiguationData":[OD(1.0)],"derivedFrom":[subQ1,subQ0]});Q7=makeQuery(id+"F3.imprint","IMPRINT",FACE,{"disambiguationData":[TD([[makeQuery(id+"F3.imprint","IMPRINT",EDGE,{"disambiguationData":[TD([[subQ2,-1.0]])],"derivedFrom":subQ1}),1.0]])]});}
            var Q8;
            {var subQ0=sQuery(id+"F3.wireOp",EDGE,"E115.top");var subQ1=sQuery(id+"F3.wireOp",EDGE,"E114");var subQ2=makeQuery(id+"F3.imprint","INTERSECT",VERTEX,{"disambiguationData":[OD(0.0)],"derivedFrom":[subQ1,subQ0]});Q8=makeQuery(id+"F3.imprint","IMPRINT",FACE,{"disambiguationData":[TD([[makeQuery(id+"F3.imprint","IMPRINT",EDGE,{"disambiguationData":[TD([[subQ2,-1.0]])],"derivedFrom":subQ1}),1.0]])]});}
            extrude(context, id + "F4", {"entities" : qUnion([Q0, Q1, Q2, Q3, Q4, Q5, Q6, Q7, Q8]), "operationType" : NewBodyOperationType.ADD, "depth" : 15.88 * mm});
        }
        {
            var Q0;
            Q0=qCreatedBy(makeId("Top.planeOp"),FACE);
            var Q1;
            Q1=qCreatedBy(makeId("Top.planeOp"),FACE);
            var sketch = newSketch(context, id + "F5", { "sketchPlane" : qUnion([Q0, Q1])});
            skLineSegment(sketch, "E117", {"start": v(0, 0) * mm, "end": v(0, -20.32) * mm});
            skCircle(sketch, "E118", {"center": v(0, -20.32) * mm, "radius": 0.89 * mm});
            skSolve(sketch);
        }
        {
            var Q0;
            Q0=makeQuery(id+"F5.imprint","IMPRINT",FACE,{"disambiguationData":[TD([[makeQuery(id+"F5.imprint","IMPRINT",EDGE,{"derivedFrom":sQuery(id+"F5.wireOp",EDGE,"E118")}),1.0]])]});
            extrude(context, id + "F6", {"entities" : qUnion([Q0]), "operationType" : NewBodyOperationType.ADD, "depth" : 5.08 * mm, "hasSecondDirection" : true, "secondDirectionOppositeDirection" : true, "secondDirectionDepth" : 2.54 * mm});
        }
        {
            var Q0;
            Q0=makeQuery(id+"F6.opExtrude","CAP_FACE",FACE,{"disambiguationData":[OSD([sQuery(id+"F5.wireOp",EDGE,"E118")])],"isStart":false});
            var sketch = newSketch(context, id + "F7", { "sketchPlane" : qUnion([Q0])});
            skCircle(sketch, "E119", {"center": v(0, -20.32) * mm, "radius": 0.64 * mm});
            skSolve(sketch);
        }
        {
            var Q0;
            Q0 = qSketchRegion(id + "F7", true);
            extrude(context, id + "F8", {"entities" : qUnion([Q0]), "operationType" : NewBodyOperationType.REMOVE, "endBound" : BoundingType.THROUGH_ALL, "oppositeDirection" : true, "depth" : 25.4 * mm});
        }
    });
